# Revit family: Deca_Torneira Cozinha Link_1168.C.LNK_Bica Móvel Parede
name_source: partatom
category: Plumbing Fixtures
revit_build: Autodesk Revit Architecture 2012 (Build: 20120126_0600(x64)
units: mm (PartAtom-declared; Revit-internal decimal feet)

## types (1)
- 1168.C.LNK_Cromado CR10
    Aprovado por = Contino/quattroD
    Assembly Code = D2020
    Atendimento ao Cliente = 0800-0117073
    CWFU = 0
    Consumo = Varia com a pressão
    Criado por = Contino/quattroD
    Código = 1168.C.LNK
    Default Elevation = 800 mm  [stored 2.62467 ft]
    Description = Torneira Cozinha Parede
    Diâmetro Água Fria = 15 mm  [stored 0.0492126 ft]
    Flow Pressure = 0.00 psi
    HWFU = 0
    Informações Complementares = Mecanismo: 1/4 de volta
    Linha = Link
    Louça/Metais = Metal
    Manufacturer = Deca
    Material = Deca_Latão Cromado e Plástico de Engenharia
    Misturador = Deca CR10 Cromado Metal
    Model = 1168.C.LNK
    Norma = ABNT NBR 15748: 2009
    Peso Liquido (Kg) = 1.68
    Pressão = 2 A 40 mca
    Produto = Torneira Cozinha Bica Móvel Parede Link
    Raio Água Fria = 8 mm  [stored 0.0262467 ft]
    Segmento = Competitivo
    URL = www.deca.com.br/produtos
    Variações de COR = Cromado (1168.C.LNK)
    WFU = 0

note: [stored X ft] marks values corroborated as IEEE doubles in the binary element streams (Revit-internal decimal feet)

## geometry (parser evidence)
native form markers: Blend x4, Sweep x3
no freeform markers — native parametric forms only
